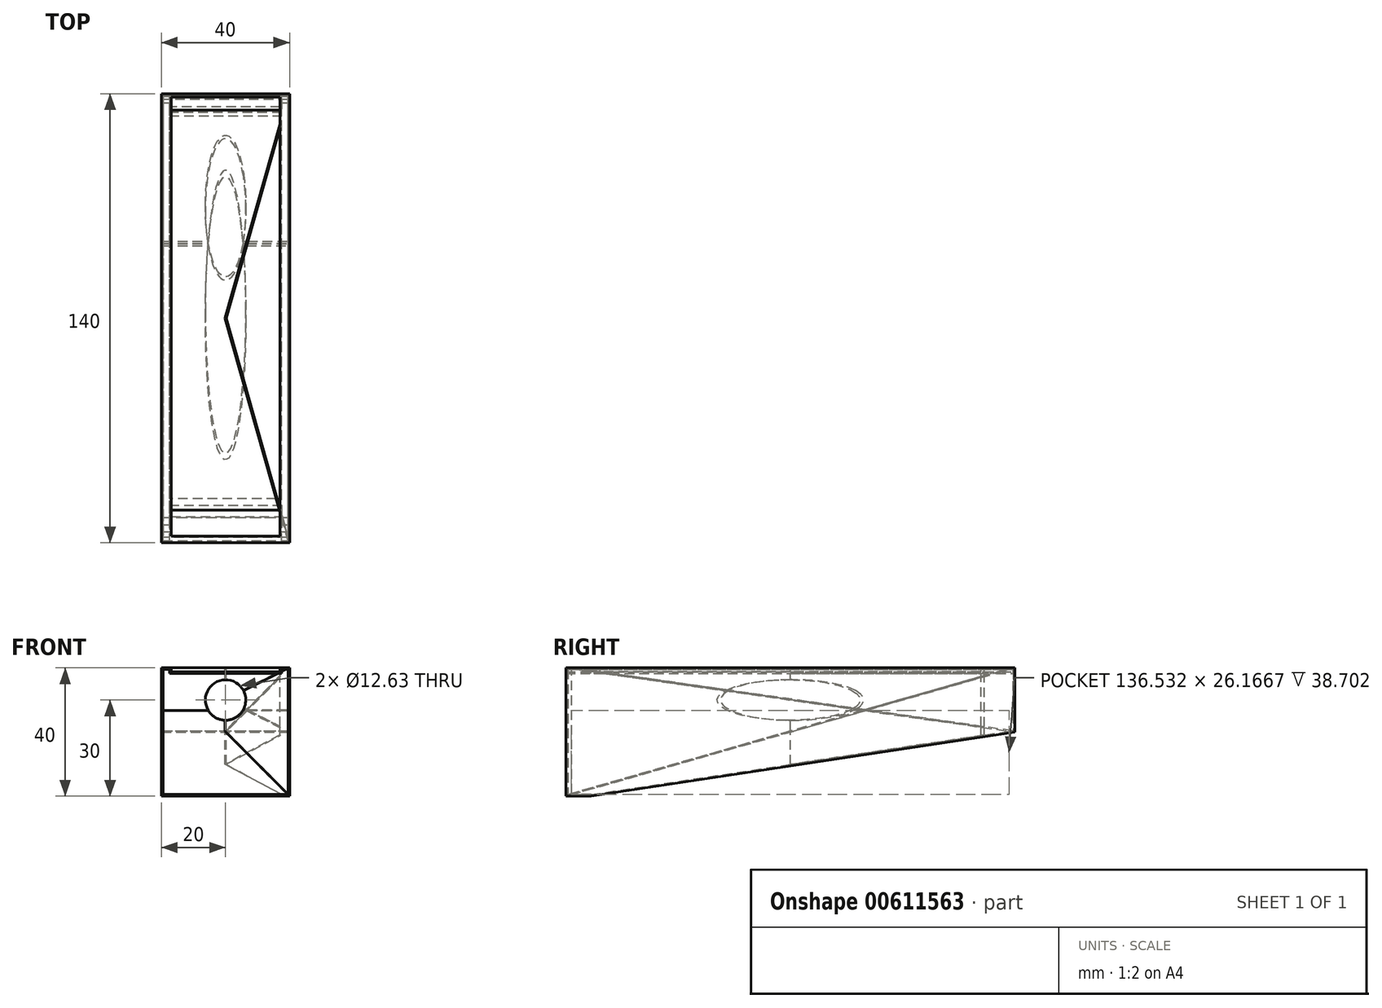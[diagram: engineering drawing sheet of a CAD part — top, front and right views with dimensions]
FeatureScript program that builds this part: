
annotation { "Feature Type Name" : "Feature", "Feature Type Description" : "" }
export const myFeature = defineFeature(function(context is Context, id is Id, definition is map)
    precondition{}
    {
        {
            var Q0;
            Q0=qCreatedBy(makeId("Front.planeOp"),FACE);
            var sketch = newSketch(context, id + "F0", { "sketchPlane" : qUnion([Q0])});
            skLineSegment(sketch, "E0.bottom", {"start": v(-15, 20) * mm, "end": v(15, 20) * mm});
            skLineSegment(sketch, "E0.top", {"start": v(-15, -20) * mm, "end": v(15, -20) * mm});
            skLineSegment(sketch, "E0.left", {"start": v(-20, 15) * mm, "end": v(-20, -15) * mm});
            skLineSegment(sketch, "E0.right", {"start": v(20, 15) * mm, "end": v(20, -15) * mm});
            skPoint(sketch, "E0.middle", {"position": v(0, 0) * mm});
            skPoint(sketch, "E1.visualSharp", {"position": v(-20, -20) * mm});
            skPoint(sketch, "E2.visualSharp", {"position": v(20, -20) * mm});
            skLineSegment(sketch, "E3", {"start": v(-20, -15) * mm, "end": v(20, -15) * mm});
            skLineSegment(sketch, "E4", {"start": v(-20, -15) * mm, "end": v(-20, -11.86) * mm});
            skLineSegment(sketch, "E5", {"start": v(-20, -15) * mm, "end": v(-17, -15) * mm});
            skLineSegment(sketch, "E6", {"start": v(-17, -15) * mm, "end": v(-17, 20) * mm});
            skLineSegment(sketch, "E7", {"start": v(-17, 20) * mm, "end": v(-17, 15) * mm});
            skLineSegment(sketch, "E8", {"start": v(-17, 15) * mm, "end": v(-20, 15) * mm});
            skLineSegment(sketch, "E9.MirrorCS", {"start": v(17, -15) * mm, "end": v(17, 20) * mm});
            skLineSegment(sketch, "E10.MirrorCS", {"start": v(20, 20) * mm, "end": v(20, -15) * mm});
            skLineSegment(sketch, "E11.MirrorCS", {"start": v(17, 15) * mm, "end": v(20, 15) * mm});
            skLineSegment(sketch, "E12", {"start": v(-18.5, 15) * mm, "end": v(-18.5, -15) * mm});
            skLineSegment(sketch, "E13", {"start": v(-18.5, -5.26) * mm, "end": v(-18.5, -3.26) * mm});
            skLineSegment(sketch, "E14", {"start": v(-18.5, 2.74) * mm, "end": v(-18.5, 4.74) * mm});
            skLineSegment(sketch, "E15", {"start": v(-15, -20) * mm, "end": v(-15, -15) * mm});
            skLineSegment(sketch, "E16", {"start": v(-15, -17.5) * mm, "end": v(15, -17.5) * mm});
            skLineSegment(sketch, "E17", {"start": v(15, -17.5) * mm, "end": v(15, -20) * mm});
            skLineSegment(sketch, "E18", {"start": v(15, -17.5) * mm, "end": v(15, -15) * mm});
            skLineSegment(sketch, "E19", {"start": v(-15, -15) * mm, "end": v(-18.54, -18.54) * mm});
            skLineSegment(sketch, "E20", {"start": v(-18.54, -18.54) * mm, "end": v(-16.77, -16.77) * mm});
            skLineSegment(sketch, "E21", {"start": v(-20, -15) * mm, "end": v(-15, -20) * mm});
            skCircle(sketch, "E22", {"center": v(0, -17.5) * mm, "radius": 2.07 * mm});
            skCircle(sketch, "E23", {"center": v(-10.25, -17.5) * mm, "radius": 1.14 * mm});
            skCircle(sketch, "E24", {"center": v(-5.95, -17.5) * mm, "radius": 1.97 * mm});
            skCircle(sketch, "E25.MirrorC", {"center": v(5.95, -17.5) * mm, "radius": 1.97 * mm});
            skCircle(sketch, "E26.MirrorC", {"center": v(10.25, -17.5) * mm, "radius": 1.14 * mm});
            skLineSegment(sketch, "E27", {"start": v(-17, 20) * mm, "end": v(17, 20) * mm});
            skPoint(sketch, "E28.visualSharp", {"position": v(-20, 20) * mm});
            skPoint(sketch, "E29.visualSharp", {"position": v(20, 20) * mm});
            skLineSegment(sketch, "E30", {"start": v(-17, 17.5) * mm, "end": v(17, 17.5) * mm});
            skLineSegment(sketch, "E31", {"start": v(-17, 18.83) * mm, "end": v(17, 18.83) * mm});
            skLineSegment(sketch, "E32", {"start": v(-20, 15) * mm, "end": v(-20, 20) * mm});
            skLineSegment(sketch, "E33", {"start": v(17, 20) * mm, "end": v(20, 20) * mm});
            skLineSegment(sketch, "E34", {"start": v(-20, 20) * mm, "end": v(-17, 20) * mm});
            skLineSegment(sketch, "E35", {"start": v(15, -20) * mm, "end": v(20, -20) * mm});
            skLineSegment(sketch, "E36", {"start": v(20, -15) * mm, "end": v(20, -20) * mm});
            skLineSegment(sketch, "E37", {"start": v(-15, -20) * mm, "end": v(-20, -20) * mm});
            skLineSegment(sketch, "E38", {"start": v(-20, -15) * mm, "end": v(-20, -20) * mm});
            skSolve(sketch);
        }
        {
            var Q0;
            {var subQ5=sQuery(id+"F0.wireOp",EDGE,"E11.MirrorCS");Q0=makeQuery(id+"F0.imprint","IMPRINT",FACE,{"disambiguationData":[TD([[makeQuery(id+"F0.imprint","IMPRINT",EDGE,{"derivedFrom":subQ5}),1.0]])]});}
            var Q1;
            {var subQ0=sQuery(id+"F0.wireOp",EDGE,"E21");var subQ3=sQuery(id+"F0.wireOp",EDGE,"kyP0Ghf2-8tRf-b2os-GJ9Y-R51s7YL5zU5A");var subQ5=makeQuery(id+"F0.imprint","INTERSECT",VERTEX,{"disambiguationData":[OD(0.0)],"derivedFrom":[subQ0,subQ3]});Q1=makeQuery(id+"F0.imprint","IMPRINT",FACE,{"disambiguationData":[TD([[makeQuery(id+"F0.imprint","IMPRINT",EDGE,{"disambiguationData":[TD([[subQ5,-1.0]])],"derivedFrom":subQ3}),-1.0]])]});}
            var Q2;
            {var subQ0=sQuery(id+"F0.wireOp",EDGE,"E21");var subQ3=sQuery(id+"F0.wireOp",EDGE,"kyP0Ghf2-8tRf-b2os-GJ9Y-R51s7YL5zU5A");var subQ5=makeQuery(id+"F0.imprint","INTERSECT",VERTEX,{"disambiguationData":[OD(1.0)],"derivedFrom":[subQ0,subQ3]});Q2=makeQuery(id+"F0.imprint","IMPRINT",FACE,{"disambiguationData":[TD([[makeQuery(id+"F0.imprint","IMPRINT",EDGE,{"disambiguationData":[TD([[subQ5,1.0]])],"derivedFrom":subQ3}),-1.0]])]});}
            var Q3;
            {var subQ1=sQuery(id+"F0.wireOp",EDGE,"E2.filletArc");var subQ3=sQuery(id+"F0.wireOp",EDGE,"8bdb658c-147e-4b0e-9f76-7d081b696ae10.MirrorC");var subQ4=makeQuery(id+"F0.imprint","INTERSECT",VERTEX,{"derivedFrom":[subQ1,subQ3]});Q3=makeQuery(id+"F0.imprint","IMPRINT",FACE,{"disambiguationData":[TD([[makeQuery(id+"F0.imprint","IMPRINT",EDGE,{"disambiguationData":[TD([[subQ4,-1.0]])],"derivedFrom":subQ3}),1.0]])]});}
            var Q4;
            {var subQ1=sQuery(id+"F0.wireOp",EDGE,"E2.filletArc");var subQ3=sQuery(id+"F0.wireOp",EDGE,"8bdb658c-147e-4b0e-9f76-7d081b696ae10.MirrorC");var subQ4=makeQuery(id+"F0.imprint","INTERSECT",VERTEX,{"derivedFrom":[subQ1,subQ3]});Q4=makeQuery(id+"F0.imprint","IMPRINT",FACE,{"disambiguationData":[TD([[makeQuery(id+"F0.imprint","IMPRINT",EDGE,{"disambiguationData":[TD([[subQ4,1.0]])],"derivedFrom":subQ3}),1.0]])]});}
            var Q5;
            {var subQ0=sQuery(id+"F0.wireOp",EDGE,"E7");Q5=makeQuery(id+"F0.imprint","IMPRINT",FACE,{"disambiguationData":[TD([[makeQuery(id+"F0.imprint","IMPRINT",EDGE,{"derivedFrom":subQ0}),-1.0]])]});}
            var Q6;
            {var subQ0=sQuery(id+"F0.wireOp",EDGE,"E8");var subQ1=sQuery(id+"F0.wireOp",EDGE,"E0.left");var subQ2=makeQuery(id+"F0.imprint","INTERSECT",VERTEX,{"derivedFrom":[subQ1,subQ0]});Q6=makeQuery(id+"F0.imprint","IMPRINT",FACE,{"disambiguationData":[TD([[makeQuery(id+"F0.imprint","IMPRINT",EDGE,{"disambiguationData":[TD([[subQ2,-1.0]])],"derivedFrom":subQ1}),1.0]])]});}
            var Q7;
            {var subQ0=sQuery(id+"F0.wireOp",EDGE,"1121410c-8889-4fde-b7d4-53cf977519030.MirrorC");var subQ1=sQuery(id+"F0.wireOp",EDGE,"E0.left");var subQ2=makeQuery(id+"F0.imprint","INTERSECT",VERTEX,{"derivedFrom":[subQ1,subQ0]});Q7=makeQuery(id+"F0.imprint","IMPRINT",FACE,{"disambiguationData":[TD([[makeQuery(id+"F0.imprint","IMPRINT",EDGE,{"disambiguationData":[TD([[subQ2,-1.0]])],"derivedFrom":subQ1}),1.0]])]});}
            var Q8;
            {var subQ1=sQuery(id+"F0.wireOp",EDGE,"E0.left");var subQ5=sQuery(id+"F0.wireOp",EDGE,"3be5d0f7-e66a-4034-bf2c-b5a2b3a159480.MirrorC");var subQ6=makeQuery(id+"F0.imprint","INTERSECT",VERTEX,{"derivedFrom":[subQ1,subQ5]});Q8=makeQuery(id+"F0.imprint","IMPRINT",FACE,{"disambiguationData":[TD([[makeQuery(id+"F0.imprint","IMPRINT",EDGE,{"disambiguationData":[TD([[subQ6,-1.0]])],"derivedFrom":subQ1}),1.0]])]});}
            var Q9;
            {var subQ0=sQuery(id+"F0.wireOp",EDGE,"fb5a3924-ac59-4bed-af84-7003ddc445cf0.MirrorC");var subQ1=sQuery(id+"F0.wireOp",EDGE,"E0.left");var subQ2=makeQuery(id+"F0.imprint","INTERSECT",VERTEX,{"derivedFrom":[subQ1,subQ0]});Q9=makeQuery(id+"F0.imprint","IMPRINT",FACE,{"disambiguationData":[TD([[makeQuery(id+"F0.imprint","IMPRINT",EDGE,{"disambiguationData":[TD([[subQ2,-1.0]])],"derivedFrom":subQ1}),1.0]])]});}
            var Q10;
            {var subQ1=sQuery(id+"F0.wireOp",EDGE,"E0.left");var subQ7=sQuery(id+"F0.wireOp",EDGE,"804b6b5c-8591-4f70-8d60-dec1e7231a500.MirrorC");var subQ9=makeQuery(id+"F0.imprint","INTERSECT",VERTEX,{"derivedFrom":[subQ1,subQ7]});Q10=makeQuery(id+"F0.imprint","IMPRINT",FACE,{"disambiguationData":[TD([[makeQuery(id+"F0.imprint","IMPRINT",EDGE,{"disambiguationData":[TD([[subQ9,-1.0]])],"derivedFrom":subQ1}),1.0]])]});}
            var Q11;
            {var subQ0=sQuery(id+"F0.wireOp",EDGE,"UupdKjqE-uhdA-a4V7-ZC8J-dwgjoSrKTdi6");var subQ1=sQuery(id+"F0.wireOp",EDGE,"E0.left");var subQ2=makeQuery(id+"F0.imprint","INTERSECT",VERTEX,{"derivedFrom":[subQ1,subQ0]});Q11=makeQuery(id+"F0.imprint","IMPRINT",FACE,{"disambiguationData":[TD([[makeQuery(id+"F0.imprint","IMPRINT",EDGE,{"disambiguationData":[TD([[subQ2,-1.0]])],"derivedFrom":subQ1}),1.0]])]});}
            var Q12;
            {var subQ1=sQuery(id+"F0.wireOp",EDGE,"E5");var subQ3=sQuery(id+"F0.wireOp",EDGE,"kyP0Ghf2-8tRf-b2os-GJ9Y-R51s7YL5zU5A");var subQ4=makeQuery(id+"F0.imprint","INTERSECT",VERTEX,{"derivedFrom":[subQ1,subQ3]});Q12=makeQuery(id+"F0.imprint","IMPRINT",FACE,{"disambiguationData":[TD([[makeQuery(id+"F0.imprint","IMPRINT",EDGE,{"disambiguationData":[TD([[subQ4,-1.0]])],"derivedFrom":subQ3}),-1.0]])]});}
            var Q13;
            {var subQ0=sQuery(id+"F0.wireOp",EDGE,"819de83c-ce93-4df8-b3f5-d03e4e11402c4.MirrorC");var subQ1=sQuery(id+"F0.wireOp",EDGE,"E9.MirrorCS");var subQ2=makeQuery(id+"F0.imprint","INTERSECT",VERTEX,{"derivedFrom":[subQ1,subQ0]});Q13=makeQuery(id+"F0.imprint","IMPRINT",FACE,{"disambiguationData":[TD([[makeQuery(id+"F0.imprint","IMPRINT",EDGE,{"disambiguationData":[TD([[subQ2,-1.0]])],"derivedFrom":subQ1}),-1.0]])]});}
            var Q14;
            {var subQ0=sQuery(id+"F0.wireOp",EDGE,"819de83c-ce93-4df8-b3f5-d03e4e11402c3.MirrorC");var subQ1=sQuery(id+"F0.wireOp",EDGE,"E9.MirrorCS");var subQ2=makeQuery(id+"F0.imprint","INTERSECT",VERTEX,{"derivedFrom":[subQ1,subQ0]});Q14=makeQuery(id+"F0.imprint","IMPRINT",FACE,{"disambiguationData":[TD([[makeQuery(id+"F0.imprint","IMPRINT",EDGE,{"disambiguationData":[TD([[subQ2,-1.0]])],"derivedFrom":subQ1}),-1.0]])]});}
            var Q15;
            {var subQ0=sQuery(id+"F0.wireOp",EDGE,"819de83c-ce93-4df8-b3f5-d03e4e11402c7.MirrorC");var subQ1=sQuery(id+"F0.wireOp",EDGE,"E9.MirrorCS");var subQ2=makeQuery(id+"F0.imprint","INTERSECT",VERTEX,{"derivedFrom":[subQ1,subQ0]});Q15=makeQuery(id+"F0.imprint","IMPRINT",FACE,{"disambiguationData":[TD([[makeQuery(id+"F0.imprint","IMPRINT",EDGE,{"disambiguationData":[TD([[subQ2,-1.0]])],"derivedFrom":subQ1}),-1.0]])]});}
            var Q16;
            {var subQ0=sQuery(id+"F0.wireOp",EDGE,"819de83c-ce93-4df8-b3f5-d03e4e11402c8.MirrorC");var subQ1=sQuery(id+"F0.wireOp",EDGE,"E9.MirrorCS");var subQ2=makeQuery(id+"F0.imprint","INTERSECT",VERTEX,{"derivedFrom":[subQ1,subQ0]});Q16=makeQuery(id+"F0.imprint","IMPRINT",FACE,{"disambiguationData":[TD([[makeQuery(id+"F0.imprint","IMPRINT",EDGE,{"disambiguationData":[TD([[subQ2,-1.0]])],"derivedFrom":subQ1}),-1.0]])]});}
            var Q17;
            {var subQ0=sQuery(id+"F0.wireOp",EDGE,"819de83c-ce93-4df8-b3f5-d03e4e11402c5.MirrorC");var subQ1=sQuery(id+"F0.wireOp",EDGE,"E9.MirrorCS");var subQ2=makeQuery(id+"F0.imprint","INTERSECT",VERTEX,{"derivedFrom":[subQ1,subQ0]});Q17=makeQuery(id+"F0.imprint","IMPRINT",FACE,{"disambiguationData":[TD([[makeQuery(id+"F0.imprint","IMPRINT",EDGE,{"disambiguationData":[TD([[subQ2,-1.0]])],"derivedFrom":subQ1}),-1.0]])]});}
            var Q18;
            {var subQ0=sQuery(id+"F0.wireOp",EDGE,"E11.MirrorCS");Q18=makeQuery(id+"F0.imprint","IMPRINT",FACE,{"disambiguationData":[TD([[makeQuery(id+"F0.imprint","IMPRINT",EDGE,{"derivedFrom":subQ0}),-1.0]])]});}
            var Q19;
            {var subQ1=sQuery(id+"F0.wireOp",EDGE,"E15");var subQ3=sQuery(id+"F0.wireOp",EDGE,"kyP0Ghf2-8tRf-b2os-GJ9Y-R51s7YL5zU5A");var subQ4=makeQuery(id+"F0.imprint","INTERSECT",VERTEX,{"derivedFrom":[subQ1,subQ3]});Q19=makeQuery(id+"F0.imprint","IMPRINT",FACE,{"disambiguationData":[TD([[makeQuery(id+"F0.imprint","IMPRINT",EDGE,{"disambiguationData":[TD([[subQ4,1.0]])],"derivedFrom":subQ3}),-1.0]])]});}
            var Q20;
            {var subQ1=sQuery(id+"F0.wireOp",EDGE,"E4");Q20=makeQuery(id+"F0.imprint","IMPRINT",FACE,{"disambiguationData":[TD([[makeQuery(id+"F0.imprint","IMPRINT",EDGE,{"derivedFrom":subQ1}),-1.0]])]});}
            var Q21;
            {var subQ3=sQuery(id+"F0.wireOp",EDGE,"E9.MirrorCS");var subQ5=sQuery(id+"F0.wireOp",EDGE,"8bdb658c-147e-4b0e-9f76-7d081b696ae10.MirrorC");var subQ8=makeQuery(id+"F0.imprint","INTERSECT",VERTEX,{"derivedFrom":[subQ3,subQ5]});Q21=makeQuery(id+"F0.imprint","IMPRINT",FACE,{"disambiguationData":[TD([[makeQuery(id+"F0.imprint","IMPRINT",EDGE,{"disambiguationData":[TD([[subQ8,-1.0]])],"derivedFrom":subQ3}),-1.0]])]});}
            var Q22;
            {var subQ1=sQuery(id+"F0.wireOp",EDGE,"E0.top");Q22=makeQuery(id+"F0.imprint","IMPRINT",FACE,{"disambiguationData":[TD([[makeQuery(id+"F0.imprint","IMPRINT",EDGE,{"derivedFrom":subQ1}),1.0]])]});}
            var Q23;
            {var subQ0=sQuery(id+"F0.wireOp",EDGE,"E18");Q23=makeQuery(id+"F0.imprint","IMPRINT",FACE,{"disambiguationData":[TD([[makeQuery(id+"F0.imprint","IMPRINT",EDGE,{"derivedFrom":subQ0}),-1.0]])]});}
            var Q24;
            {var subQ0=sQuery(id+"F0.wireOp",EDGE,"E8");var subQ5=sQuery(id+"F0.wireOp",EDGE,"E12");var subQ7=makeQuery(id+"F0.imprint","INTERSECT",VERTEX,{"derivedFrom":[subQ0,subQ5]});Q24=makeQuery(id+"F0.imprint","IMPRINT",FACE,{"disambiguationData":[TD([[makeQuery(id+"F0.imprint","IMPRINT",EDGE,{"disambiguationData":[TD([[subQ7,-1.0]])],"derivedFrom":subQ5}),1.0]])]});}
            var Q25;
            {var subQ0=sQuery(id+"F0.wireOp",EDGE,"3be5d0f7-e66a-4034-bf2c-b5a2b3a159480.MirrorC");var subQ1=sQuery(id+"F0.wireOp",EDGE,"E6");var subQ2=makeQuery(id+"F0.imprint","INTERSECT",VERTEX,{"derivedFrom":[subQ1,subQ0]});Q25=makeQuery(id+"F0.imprint","IMPRINT",FACE,{"disambiguationData":[TD([[makeQuery(id+"F0.imprint","IMPRINT",EDGE,{"disambiguationData":[TD([[subQ2,-1.0]])],"derivedFrom":subQ1}),1.0]])]});}
            var Q26;
            {var subQ3=sQuery(id+"F0.wireOp",EDGE,"fb5a3924-ac59-4bed-af84-7003ddc445cf0.MirrorC");var subQ7=sQuery(id+"F0.wireOp",EDGE,"E6");var subQ9=makeQuery(id+"F0.imprint","INTERSECT",VERTEX,{"derivedFrom":[subQ7,subQ3]});Q26=makeQuery(id+"F0.imprint","IMPRINT",FACE,{"disambiguationData":[TD([[makeQuery(id+"F0.imprint","IMPRINT",EDGE,{"disambiguationData":[TD([[subQ9,-1.0]])],"derivedFrom":subQ7}),1.0]])]});}
            var Q27;
            {var subQ0=sQuery(id+"F0.wireOp",EDGE,"804b6b5c-8591-4f70-8d60-dec1e7231a500.MirrorC");var subQ1=sQuery(id+"F0.wireOp",EDGE,"E6");var subQ2=makeQuery(id+"F0.imprint","INTERSECT",VERTEX,{"derivedFrom":[subQ1,subQ0]});Q27=makeQuery(id+"F0.imprint","IMPRINT",FACE,{"disambiguationData":[TD([[makeQuery(id+"F0.imprint","IMPRINT",EDGE,{"disambiguationData":[TD([[subQ2,-1.0]])],"derivedFrom":subQ1}),1.0]])]});}
            var Q28;
            {var subQ3=sQuery(id+"F0.wireOp",EDGE,"UupdKjqE-uhdA-a4V7-ZC8J-dwgjoSrKTdi6");var subQ5=sQuery(id+"F0.wireOp",EDGE,"E6");var subQ6=makeQuery(id+"F0.imprint","INTERSECT",VERTEX,{"derivedFrom":[subQ5,subQ3]});Q28=makeQuery(id+"F0.imprint","IMPRINT",FACE,{"disambiguationData":[TD([[makeQuery(id+"F0.imprint","IMPRINT",EDGE,{"disambiguationData":[TD([[subQ6,-1.0]])],"derivedFrom":subQ5}),1.0]])]});}
            var Q29;
            {var subQ0=sQuery(id+"F0.wireOp",EDGE,"kyP0Ghf2-8tRf-b2os-GJ9Y-R51s7YL5zU5A");var subQ5=sQuery(id+"F0.wireOp",EDGE,"E16");var subQ6=makeQuery(id+"F0.imprint","INTERSECT",VERTEX,{"derivedFrom":[subQ5,subQ0]});Q29=makeQuery(id+"F0.imprint","IMPRINT",FACE,{"disambiguationData":[TD([[makeQuery(id+"F0.imprint","IMPRINT",EDGE,{"disambiguationData":[TD([[subQ6,-1.0]])],"derivedFrom":subQ5}),1.0]])]});}
            var Q30;
            {var subQ1=sQuery(id+"F0.wireOp",EDGE,"E19");Q30=makeQuery(id+"F0.imprint","IMPRINT",FACE,{"disambiguationData":[TD([[makeQuery(id+"F0.imprint","IMPRINT",EDGE,{"derivedFrom":subQ1}),1.0]])]});}
            var Q31;
            {var subQ1=sQuery(id+"F0.wireOp",EDGE,"E1.filletArc");var subQ3=sQuery(id+"F0.wireOp",EDGE,"E20");var subQ4=makeQuery(id+"F0.imprint","INTERSECT",VERTEX,{"derivedFrom":[subQ1,subQ3]});Q31=makeQuery(id+"F0.imprint","IMPRINT",FACE,{"disambiguationData":[TD([[makeQuery(id+"F0.imprint","IMPRINT",EDGE,{"disambiguationData":[TD([[subQ4,-1.0]])],"derivedFrom":subQ3}),-1.0]])]});}
            var Q32;
            {var subQ1=sQuery(id+"F0.wireOp",EDGE,"E1.filletArc");var subQ3=sQuery(id+"F0.wireOp",EDGE,"E20");var subQ4=makeQuery(id+"F0.imprint","INTERSECT",VERTEX,{"derivedFrom":[subQ1,subQ3]});Q32=makeQuery(id+"F0.imprint","IMPRINT",FACE,{"disambiguationData":[TD([[makeQuery(id+"F0.imprint","IMPRINT",EDGE,{"disambiguationData":[TD([[subQ4,-1.0]])],"derivedFrom":subQ3}),-1.0]])]});}
            var Q33;
            {var subQ0=sQuery(id+"F0.wireOp",EDGE,"E19");Q33=makeQuery(id+"F0.imprint","IMPRINT",FACE,{"disambiguationData":[TD([[makeQuery(id+"F0.imprint","IMPRINT",EDGE,{"derivedFrom":subQ0}),-1.0]])]});}
            var Q34;
            {var subQ1=sQuery(id+"F0.wireOp",EDGE,"E1.filletArc");var subQ3=sQuery(id+"F0.wireOp",EDGE,"E20");var subQ4=makeQuery(id+"F0.imprint","INTERSECT",VERTEX,{"derivedFrom":[subQ1,subQ3]});Q34=makeQuery(id+"F0.imprint","IMPRINT",FACE,{"disambiguationData":[TD([[makeQuery(id+"F0.imprint","IMPRINT",EDGE,{"disambiguationData":[TD([[subQ4,-1.0]])],"derivedFrom":subQ3}),1.0]])]});}
            var Q35;
            {var subQ1=sQuery(id+"F0.wireOp",EDGE,"E31");var subQ14=sQuery(id+"F0.wireOp",EDGE,"E7");var subQ15=makeQuery(id+"F0.imprint","INTERSECT",VERTEX,{"derivedFrom":[subQ14,subQ1]});Q35=makeQuery(id+"F0.imprint","IMPRINT",FACE,{"disambiguationData":[TD([[makeQuery(id+"F0.imprint","IMPRINT",EDGE,{"disambiguationData":[TD([[subQ15,1.0]])],"derivedFrom":subQ14}),1.0]])]});}
            var Q36;
            {var subQ8=sQuery(id+"F0.wireOp",EDGE,"E30");Q36=makeQuery(id+"F0.imprint","IMPRINT",FACE,{"disambiguationData":[TD([[makeQuery(id+"F0.imprint","IMPRINT",EDGE,{"derivedFrom":subQ8}),1.0]])]});}
            var Q37;
            {var subQ3=sQuery(id+"F0.wireOp",EDGE,"E37");Q37=makeQuery(id+"F0.imprint","IMPRINT",FACE,{"disambiguationData":[TD([[makeQuery(id+"F0.imprint","IMPRINT",EDGE,{"derivedFrom":subQ3}),-1.0]])]});}
            var Q38;
            {var subQ0=sQuery(id+"F0.wireOp",EDGE,"E6");Q38=makeQuery(id+"F0.imprint","IMPRINT",FACE,{"disambiguationData":[TD([[makeQuery(id+"F0.imprint","IMPRINT",EDGE,{"derivedFrom":subQ0}),-1.0]])]});}
            var Q39;
            {var subQ0=sQuery(id+"F0.wireOp",EDGE,"E25.MirrorC");var subQ1=sQuery(id+"F0.wireOp",EDGE,"E16");var subQ2=makeQuery(id+"F0.imprint","INTERSECT",VERTEX,{"disambiguationData":[OD(0.0)],"derivedFrom":[subQ1,subQ0]});Q39=makeQuery(id+"F0.imprint","IMPRINT",FACE,{"disambiguationData":[TD([[makeQuery(id+"F0.imprint","IMPRINT",EDGE,{"disambiguationData":[TD([[subQ2,-1.0]])],"derivedFrom":subQ1}),1.0]])]});}
            var Q40;
            {var subQ0=sQuery(id+"F0.wireOp",EDGE,"E25.MirrorC");var subQ1=sQuery(id+"F0.wireOp",EDGE,"E16");var subQ2=makeQuery(id+"F0.imprint","INTERSECT",VERTEX,{"disambiguationData":[OD(0.0)],"derivedFrom":[subQ1,subQ0]});Q40=makeQuery(id+"F0.imprint","IMPRINT",FACE,{"disambiguationData":[TD([[makeQuery(id+"F0.imprint","IMPRINT",EDGE,{"disambiguationData":[TD([[subQ2,-1.0]])],"derivedFrom":subQ1}),-1.0]])]});}
            var Q41;
            {var subQ0=sQuery(id+"F0.wireOp",EDGE,"E26.MirrorC");var subQ1=sQuery(id+"F0.wireOp",EDGE,"E16");var subQ2=makeQuery(id+"F0.imprint","INTERSECT",VERTEX,{"disambiguationData":[OD(0.0)],"derivedFrom":[subQ1,subQ0]});Q41=makeQuery(id+"F0.imprint","IMPRINT",FACE,{"disambiguationData":[TD([[makeQuery(id+"F0.imprint","IMPRINT",EDGE,{"disambiguationData":[TD([[subQ2,-1.0]])],"derivedFrom":subQ1}),-1.0]])]});}
            var Q42;
            {var subQ0=sQuery(id+"F0.wireOp",EDGE,"E26.MirrorC");var subQ1=sQuery(id+"F0.wireOp",EDGE,"E16");var subQ2=makeQuery(id+"F0.imprint","INTERSECT",VERTEX,{"disambiguationData":[OD(0.0)],"derivedFrom":[subQ1,subQ0]});Q42=makeQuery(id+"F0.imprint","IMPRINT",FACE,{"disambiguationData":[TD([[makeQuery(id+"F0.imprint","IMPRINT",EDGE,{"disambiguationData":[TD([[subQ2,-1.0]])],"derivedFrom":subQ1}),1.0]])]});}
            var Q43;
            {var subQ0=sQuery(id+"F0.wireOp",EDGE,"E22");var subQ1=sQuery(id+"F0.wireOp",EDGE,"E16");var subQ2=makeQuery(id+"F0.imprint","INTERSECT",VERTEX,{"disambiguationData":[OD(0.0)],"derivedFrom":[subQ1,subQ0]});Q43=makeQuery(id+"F0.imprint","IMPRINT",FACE,{"disambiguationData":[TD([[makeQuery(id+"F0.imprint","IMPRINT",EDGE,{"disambiguationData":[TD([[subQ2,-1.0]])],"derivedFrom":subQ1}),1.0]])]});}
            var Q44;
            {var subQ0=sQuery(id+"F0.wireOp",EDGE,"E22");var subQ1=sQuery(id+"F0.wireOp",EDGE,"E16");var subQ2=makeQuery(id+"F0.imprint","INTERSECT",VERTEX,{"disambiguationData":[OD(0.0)],"derivedFrom":[subQ1,subQ0]});Q44=makeQuery(id+"F0.imprint","IMPRINT",FACE,{"disambiguationData":[TD([[makeQuery(id+"F0.imprint","IMPRINT",EDGE,{"disambiguationData":[TD([[subQ2,-1.0]])],"derivedFrom":subQ1}),-1.0]])]});}
            var Q45;
            {var subQ0=sQuery(id+"F0.wireOp",EDGE,"E24");var subQ1=sQuery(id+"F0.wireOp",EDGE,"E16");var subQ2=makeQuery(id+"F0.imprint","INTERSECT",VERTEX,{"disambiguationData":[OD(0.0)],"derivedFrom":[subQ1,subQ0]});Q45=makeQuery(id+"F0.imprint","IMPRINT",FACE,{"disambiguationData":[TD([[makeQuery(id+"F0.imprint","IMPRINT",EDGE,{"disambiguationData":[TD([[subQ2,-1.0]])],"derivedFrom":subQ1}),-1.0]])]});}
            var Q46;
            {var subQ0=sQuery(id+"F0.wireOp",EDGE,"E23");var subQ1=sQuery(id+"F0.wireOp",EDGE,"E16");var subQ2=makeQuery(id+"F0.imprint","INTERSECT",VERTEX,{"disambiguationData":[OD(0.0)],"derivedFrom":[subQ1,subQ0]});Q46=makeQuery(id+"F0.imprint","IMPRINT",FACE,{"disambiguationData":[TD([[makeQuery(id+"F0.imprint","IMPRINT",EDGE,{"disambiguationData":[TD([[subQ2,-1.0]])],"derivedFrom":subQ1}),1.0]])]});}
            extrude(context, id + "F1", {"entities" : qUnion([Q0, Q1, Q2, Q3, Q4, Q5, Q6, Q7, Q8, Q9, Q10, Q11, Q12, Q13, Q14, Q15, Q16, Q17, Q18, Q19, Q20, Q21, Q22, Q23, Q24, Q25, Q26, Q27, Q28, Q29, Q30, Q31, Q32, Q33, Q34, Q35, Q36, Q37, Q38, Q39, Q40, Q41, Q42, Q43, Q44, Q45, Q46]), "depth" : 140 * mm, "offsetDistance" : 25 * mm});
        }
        {
            var Q0;
            Q0=makeQuery(id+"F1.opExtrude","SWEPT_FACE",FACE,{"disambiguationData":[OSD([sQuery(id+"F0.wireOp",EDGE,"E10.MirrorCS"),sQuery(id+"F0.wireOp",EDGE,"E36")])]});
            var sketch = newSketch(context, id + "F2", { "sketchPlane" : qUnion([Q0])});
            skLineSegment(sketch, "E39", {"start": v(-132.04, -20) * mm, "end": v(0, 0) * mm});
            skLineSegment(sketch, "E40", {"start": v(-132.04, -20) * mm, "end": v(-133.12, -12.86) * mm});
            skLineSegment(sketch, "E41", {"start": v(-133.12, -12.86) * mm, "end": v(0, 7.3) * mm});
            skLineSegment(sketch, "E42", {"start": v(-133.12, -12.86) * mm, "end": v(-140, -13.9) * mm});
            skLineSegment(sketch, "E43", {"start": v(-132.04, -20) * mm, "end": v(-143.14, -21.68) * mm});
            skLineSegment(sketch, "E44", {"start": v(-143.14, -21.68) * mm, "end": v(-144.32, -13.9) * mm});
            skLineSegment(sketch, "E45", {"start": v(-140, -13.9) * mm, "end": v(-144.22, -14.54) * mm});
            skLineSegment(sketch, "E46", {"start": v(0, 20) * mm, "end": v(0, 0) * mm});
            skLineSegment(sketch, "E47", {"start": v(-140, 20) * mm, "end": v(-140, -20) * mm});
            skLineSegment(sketch, "E48", {"start": v(-140, -20) * mm, "end": v(-132.04, -20) * mm});
            skSolve(sketch);
        }
        {
            var Q0;
            {var subQ0=sQuery(id+"F2.wireOp",EDGE,"E39");Q0=makeQuery(id+"F2.imprint","IMPRINT",FACE,{"disambiguationData":[TD([[makeQuery(id+"F2.imprint","IMPRINT",EDGE,{"derivedFrom":subQ0}),-1.0]])]});}
            extrude(context, id + "F3", {"entities" : qUnion([Q0]), "operationType" : NewBodyOperationType.REMOVE, "oppositeDirection" : true, "depth" : 50 * mm, "offsetDistance" : 25 * mm});
        }
        {
            var Q0;
            {var subQ0=sQuery(id+"F2.wireOp",EDGE,"E39");Q0=makeQuery(id+"F2.imprint","IMPRINT",FACE,{"disambiguationData":[TD([[makeQuery(id+"F2.imprint","IMPRINT",EDGE,{"derivedFrom":subQ0}),1.0]])]});}
            var Q1;
            {var subQ0=sQuery(id+"F2.wireOp",EDGE,"E40");Q1=makeQuery(id+"F2.imprint","IMPRINT",FACE,{"disambiguationData":[TD([[makeQuery(id+"F2.imprint","IMPRINT",EDGE,{"derivedFrom":subQ0}),1.0]])]});}
            extrude(context, id + "F4", {"entities" : qUnion([Q0, Q1]), "operationType" : NewBodyOperationType.ADD, "oppositeDirection" : true, "depth" : 40 * mm, "offsetDistance" : 25 * mm});
        }
        {
            var Q0;
            Q0=makeQuery(id+"F4.boolean.opBoolean","MERGE",FACE,{"derivedFrom":[makeQuery(id+"F1.opExtrude","CAP_FACE",FACE,{"disambiguationData":[OSD([sQuery(id+"F0.wireOp",EDGE,"E0.top"),sQuery(id+"F0.wireOp",EDGE,"E0.left"),sQuery(id+"F0.wireOp",EDGE,"E4"),sQuery(id+"F0.wireOp",EDGE,"E10.MirrorCS"),sQuery(id+"F0.wireOp",EDGE,"E16"),sQuery(id+"F0.wireOp",EDGE,"E23"),sQuery(id+"F0.wireOp",EDGE,"E24"),sQuery(id+"F0.wireOp",EDGE,"E27"),sQuery(id+"F0.wireOp",EDGE,"E32"),sQuery(id+"F0.wireOp",EDGE,"E33"),sQuery(id+"F0.wireOp",EDGE,"E34"),sQuery(id+"F0.wireOp",EDGE,"E35"),sQuery(id+"F0.wireOp",EDGE,"E36"),sQuery(id+"F0.wireOp",EDGE,"E37"),sQuery(id+"F0.wireOp",EDGE,"E38")])],"isStart":false}),makeQuery(id+"F4.opExtrude","SWEPT_FACE",FACE,{"disambiguationData":[OSD([sQuery(id+"F2.wireOp",EDGE,"E47")])]})]});
            var Q1;
            Q1=makeQuery(id+"F1.opExtrude","SWEPT_BODY",BODY,{"disambiguationData":[OSD([sQuery(id+"F0.wireOp",EDGE,"E0.top"),sQuery(id+"F0.wireOp",EDGE,"E0.left"),sQuery(id+"F0.wireOp",EDGE,"E4"),sQuery(id+"F0.wireOp",EDGE,"E10.MirrorCS"),sQuery(id+"F0.wireOp",EDGE,"E16"),sQuery(id+"F0.wireOp",EDGE,"E23"),sQuery(id+"F0.wireOp",EDGE,"E24"),sQuery(id+"F0.wireOp",EDGE,"E27"),sQuery(id+"F0.wireOp",EDGE,"E32"),sQuery(id+"F0.wireOp",EDGE,"E33"),sQuery(id+"F0.wireOp",EDGE,"E34"),sQuery(id+"F0.wireOp",EDGE,"E35"),sQuery(id+"F0.wireOp",EDGE,"E36"),sQuery(id+"F0.wireOp",EDGE,"E37"),sQuery(id+"F0.wireOp",EDGE,"E38")])]});
            shell(context, id + "F5", {"entities" : qUnion([Q0]), "parts" : qUnion([Q1]), "thickness" : 0.5 * mm});
        }
        {
            var Q0;
            Q0=makeQuery(id+"F1.opExtrude","SWEPT_FACE",FACE,{"disambiguationData":[OSD([sQuery(id+"F0.wireOp",EDGE,"E27"),sQuery(id+"F0.wireOp",EDGE,"E33"),sQuery(id+"F0.wireOp",EDGE,"E34")])]});
            var sketch = newSketch(context, id + "F6", { "sketchPlane" : qUnion([Q0])});
            skLineSegment(sketch, "E49", {"start": v(-20, 0) * mm, "end": v(19.7, -140) * mm});
            skLineSegment(sketch, "E50", {"start": v(19.7, -140) * mm, "end": v(20, -140) * mm});
            skLineSegment(sketch, "E51", {"start": v(20, -140) * mm, "end": v(-19.7, 0) * mm});
            skLineSegment(sketch, "E52.MirrorCS", {"start": v(20, 0) * mm, "end": v(-19.7, -140) * mm});
            skLineSegment(sketch, "E53.MirrorCS", {"start": v(-20, -140) * mm, "end": v(19.7, 0) * mm});
            skLineSegment(sketch, "E54", {"start": v(-0.15, -70) * mm, "end": v(0.15, -70) * mm});
            skLineSegment(sketch, "E55", {"start": v(0.15, -70) * mm, "end": v(0, -70) * mm});
            skLineSegment(sketch, "E56", {"start": v(0, -70) * mm, "end": v(0, -70.1) * mm});
            skSolve(sketch);
        }
        {
            var Q0;
            Q0 = qSketchRegion(id + "F6", true);
            var Q1;
            {var subQ1=sQuery(id+"F6.wireOp",EDGE,"E49");var subQ3=sQuery(id+"F6.wireOp",EDGE,"E52.MirrorCS");var subQ4=makeQuery(id+"F6.imprint","INTERSECT",VERTEX,{"derivedFrom":[subQ1,subQ3]});Q1=makeQuery(id+"F6.imprint","IMPRINT",FACE,{"disambiguationData":[TD([[makeQuery(id+"F6.imprint","IMPRINT",EDGE,{"disambiguationData":[TD([[subQ4,1.0]])],"derivedFrom":subQ1}),-1.0]])]});}
            var Q2;
            {var subQ1=sQuery(id+"F6.wireOp",EDGE,"E51");var subQ3=sQuery(id+"F6.wireOp",EDGE,"E53.MirrorCS");var subQ4=makeQuery(id+"F6.imprint","INTERSECT",VERTEX,{"derivedFrom":[subQ1,subQ3]});Q2=makeQuery(id+"F6.imprint","IMPRINT",FACE,{"disambiguationData":[TD([[makeQuery(id+"F6.imprint","IMPRINT",EDGE,{"disambiguationData":[TD([[subQ4,1.0]])],"derivedFrom":subQ1}),-1.0]])]});}
            var Q3;
            {var subQ4=sQuery(id+"F6.wireOp",EDGE,"E53.MirrorCS");var subQ6=sQuery(id+"F6.wireOp",EDGE,"E51");var subQ8=makeQuery(id+"F6.imprint","INTERSECT",VERTEX,{"derivedFrom":[subQ6,subQ4]});Q3=makeQuery(id+"F6.imprint","IMPRINT",FACE,{"disambiguationData":[TD([[makeQuery(id+"F6.imprint","IMPRINT",EDGE,{"disambiguationData":[TD([[subQ8,1.0]])],"derivedFrom":subQ4}),1.0]])]});}
            var Q4;
            {var subQ0=sQuery(id+"F2.wireOp",EDGE,"E39");Q4=makeQuery(id+"F4.boolean.opBoolean","MERGE",FACE,{"derivedFrom":[makeQuery(id+"F3.boolean.opBoolean","COPY",FACE,{"derivedFrom":makeQuery(id+"F3.opExtrude","SWEPT_FACE",FACE,{"disambiguationData":[OSD([subQ0])]})}),makeQuery(id+"F4.opExtrude","SWEPT_FACE",FACE,{"disambiguationData":[OSD([subQ0])]})]});}
            extrude(context, id + "F7", {"entities" : qUnion([Q0, Q1, Q2, Q3]), "operationType" : NewBodyOperationType.ADD, "endBound" : BoundingType.UP_TO_SURFACE, "oppositeDirection" : true, "depth" : 25 * mm, "endBoundEntityFace" : qUnion([Q4]), "offsetDistance" : 25 * mm});
        }
        {
            var Q0;
            Q0=makeQuery(id+"F1.opExtrude","SWEPT_FACE",FACE,{"disambiguationData":[OSD([sQuery(id+"F0.wireOp",EDGE,"E10.MirrorCS"),sQuery(id+"F0.wireOp",EDGE,"E36")])]});
            var sketch = newSketch(context, id + "F8", { "sketchPlane" : qUnion([Q0])});
            skLineSegment(sketch, "E57", {"start": v(-140, -20) * mm, "end": v(0, 20) * mm});
            skLineSegment(sketch, "E58", {"start": v(0, 20) * mm, "end": v(-1.06, 20) * mm});
            skLineSegment(sketch, "E59", {"start": v(-1.06, 20) * mm, "end": v(-140, -19.7) * mm});
            skLineSegment(sketch, "E60", {"start": v(-140, 20) * mm, "end": v(0, 0) * mm});
            skLineSegment(sketch, "E61", {"start": v(0, 0.3) * mm, "end": v(-137.95, 20) * mm});
            skSolve(sketch);
        }
        {
            var Q0;
            Q0 = qSketchRegion(id + "F8", true);
            var Q1;
            {var subQ0=sQuery(id+"F8.wireOp",EDGE,"E61");var subQ1=sQuery(id+"F8.wireOp",EDGE,"E59");var subQ2=makeQuery(id+"F8.imprint","INTERSECT",VERTEX,{"derivedFrom":[subQ1,subQ0]});Q1=makeQuery(id+"F8.imprint","IMPRINT",FACE,{"disambiguationData":[TD([[makeQuery(id+"F8.imprint","IMPRINT",EDGE,{"disambiguationData":[TD([[subQ2,-1.0]])],"derivedFrom":subQ1}),-1.0]])]});}
            var Q2;
            {var subQ0=sQuery(id+"F8.wireOp",EDGE,"E60");var subQ1=sQuery(id+"F8.wireOp",EDGE,"E57");var subQ2=makeQuery(id+"F8.imprint","INTERSECT",VERTEX,{"derivedFrom":[subQ1,subQ0]});Q2=makeQuery(id+"F8.imprint","IMPRINT",FACE,{"disambiguationData":[TD([[makeQuery(id+"F8.imprint","IMPRINT",EDGE,{"disambiguationData":[TD([[subQ2,-1.0]])],"derivedFrom":subQ1}),-1.0]])]});}
            var Q3;
            {var subQ0=sQuery(id+"F8.wireOp",EDGE,"E57");var subQ4=sQuery(id+"F8.wireOp",EDGE,"E60");var subQ5=makeQuery(id+"F8.imprint","INTERSECT",VERTEX,{"derivedFrom":[subQ0,subQ4]});Q3=makeQuery(id+"F8.imprint","IMPRINT",FACE,{"disambiguationData":[TD([[makeQuery(id+"F8.imprint","IMPRINT",EDGE,{"disambiguationData":[TD([[subQ5,1.0]])],"derivedFrom":subQ4}),-1.0]])]});}
            var Q4;
            Q4=makeQuery(id+"F1.opExtrude","SWEPT_FACE",FACE,{"disambiguationData":[OSD([sQuery(id+"F0.wireOp",EDGE,"E0.left"),sQuery(id+"F0.wireOp",EDGE,"E4"),sQuery(id+"F0.wireOp",EDGE,"E32"),sQuery(id+"F0.wireOp",EDGE,"E38")])]});
            extrude(context, id + "F9", {"entities" : qUnion([Q0, Q1, Q2, Q3]), "operationType" : NewBodyOperationType.ADD, "endBound" : BoundingType.UP_TO_SURFACE, "oppositeDirection" : true, "depth" : 25 * mm, "endBoundEntityFace" : qUnion([Q4]), "offsetDistance" : 25 * mm});
        }
        {
            var Q0;
            Q0=makeQuery(id+"F1.opExtrude","SWEPT_FACE",FACE,{"disambiguationData":[OSD([sQuery(id+"F0.wireOp",EDGE,"E0.left"),sQuery(id+"F0.wireOp",EDGE,"E4"),sQuery(id+"F0.wireOp",EDGE,"E32"),sQuery(id+"F0.wireOp",EDGE,"E38")])]});
            var sketch = newSketch(context, id + "F10", { "sketchPlane" : qUnion([Q0])});
            skLineSegment(sketch, "E62", {"start": v(132.04, -20) * mm, "end": v(140, -20) * mm});
            skLineSegment(sketch, "E63", {"start": v(140, -20) * mm, "end": v(141.57, -20) * mm});
            skLineSegment(sketch, "E64", {"start": v(141.57, -20) * mm, "end": v(142.03, -23.42) * mm});
            skLineSegment(sketch, "E65", {"start": v(142.03, -23.42) * mm, "end": v(132.04, -21.88) * mm});
            skLineSegment(sketch, "E66", {"start": v(132.04, -21.88) * mm, "end": v(132.04, -20) * mm});
            skSolve(sketch);
        }
        {
            var Q0;
            Q0 = qSketchRegion(id + "F10", true);
            extrude(context, id + "F11", {"entities" : qUnion([Q0]), "operationType" : NewBodyOperationType.REMOVE, "oppositeDirection" : true, "depth" : 1000 * mm, "offsetDistance" : 25 * mm});
        }
        {
            var Q0;
            Q0=makeQuery(id+"F1.opExtrude","CAP_FACE",FACE,{"disambiguationData":[OSD([sQuery(id+"F0.wireOp",EDGE,"E0.top"),sQuery(id+"F0.wireOp",EDGE,"E0.left"),sQuery(id+"F0.wireOp",EDGE,"E4"),sQuery(id+"F0.wireOp",EDGE,"E10.MirrorCS"),sQuery(id+"F0.wireOp",EDGE,"E16"),sQuery(id+"F0.wireOp",EDGE,"E23"),sQuery(id+"F0.wireOp",EDGE,"E24"),sQuery(id+"F0.wireOp",EDGE,"E27"),sQuery(id+"F0.wireOp",EDGE,"E32"),sQuery(id+"F0.wireOp",EDGE,"E33"),sQuery(id+"F0.wireOp",EDGE,"E34"),sQuery(id+"F0.wireOp",EDGE,"E35"),sQuery(id+"F0.wireOp",EDGE,"E36"),sQuery(id+"F0.wireOp",EDGE,"E37"),sQuery(id+"F0.wireOp",EDGE,"E38")])],"isStart":true});
            var sketch = newSketch(context, id + "F12", { "sketchPlane" : qUnion([Q0])});
            skCircle(sketch, "E67", {"center": v(0, 10) * mm, "radius": 6.32 * mm});
            skPoint(sketch, "E67.centerSnap0", {"position": v(20, 10) * mm});
            skSolve(sketch);
        }
        {
            var Q0;
            Q0 = qSketchRegion(id + "F12", true);
            var Q1;
            {var subQ0=sQuery(id+"F0.wireOp",EDGE,"E34");var subQ1=sQuery(id+"F0.wireOp",EDGE,"E33");var subQ2=sQuery(id+"F0.wireOp",EDGE,"E27");var subQ3=makeQuery(id+"F1.opExtrude","CAP_EDGE",EDGE,{"disambiguationData":[OSD([subQ2,subQ1,subQ0])],"isStart":false});var subQ4=sQuery(id+"F0.wireOp",EDGE,"E32");Q1=makeQuery(id+"F7.boolean.opBoolean","MERGE",FACE,{"derivedFrom":[makeQuery(id+"F4.boolean.opBoolean","MERGE",FACE,{"derivedFrom":[makeQuery(id+"F1.opExtrude","CAP_FACE",FACE,{"disambiguationData":[OSD([sQuery(id+"F0.wireOp",EDGE,"E0.top"),sQuery(id+"F0.wireOp",EDGE,"E0.left"),sQuery(id+"F0.wireOp",EDGE,"E4"),sQuery(id+"F0.wireOp",EDGE,"E10.MirrorCS"),sQuery(id+"F0.wireOp",EDGE,"E16"),sQuery(id+"F0.wireOp",EDGE,"E23"),sQuery(id+"F0.wireOp",EDGE,"E24"),subQ2,subQ4,subQ1,subQ0,sQuery(id+"F0.wireOp",EDGE,"E35"),sQuery(id+"F0.wireOp",EDGE,"E36"),sQuery(id+"F0.wireOp",EDGE,"E37"),sQuery(id+"F0.wireOp",EDGE,"E38")])],"isStart":false}),makeQuery(id+"F4.opExtrude","SWEPT_FACE",FACE,{"disambiguationData":[OSD([sQuery(id+"F2.wireOp",EDGE,"E47")])]})]}),makeQuery(id+"F7.opExtrude","SWEPT_FACE",FACE,{"disambiguationData":[OSD([sQuery(id+"F6.wireOp",EDGE,"E50")])]}),makeQuery(id+"F7.opExtrude","SWEPT_FACE",FACE,{"disambiguationData":[OSD([subQ2,subQ1,subQ0]),TDD([makeQuery(id+"F6.imprint","IMPRINT",EDGE,{"disambiguationData":[TD([[makeQuery(id+"F6.imprint","INTERSECT",VERTEX,{"derivedFrom":[subQ3,sQuery(id+"F6.wireOp",EDGE,"E52.MirrorCS")]}),1.0]])],"derivedFrom":subQ3})])]})]});}
            extrude(context, id + "F13", {"entities" : qUnion([Q0]), "operationType" : NewBodyOperationType.REMOVE, "endBound" : BoundingType.UP_TO_SURFACE, "oppositeDirection" : true, "depth" : 25 * mm, "endBoundEntityFace" : qUnion([Q1]), "offsetDistance" : 25 * mm});
        }
    });
